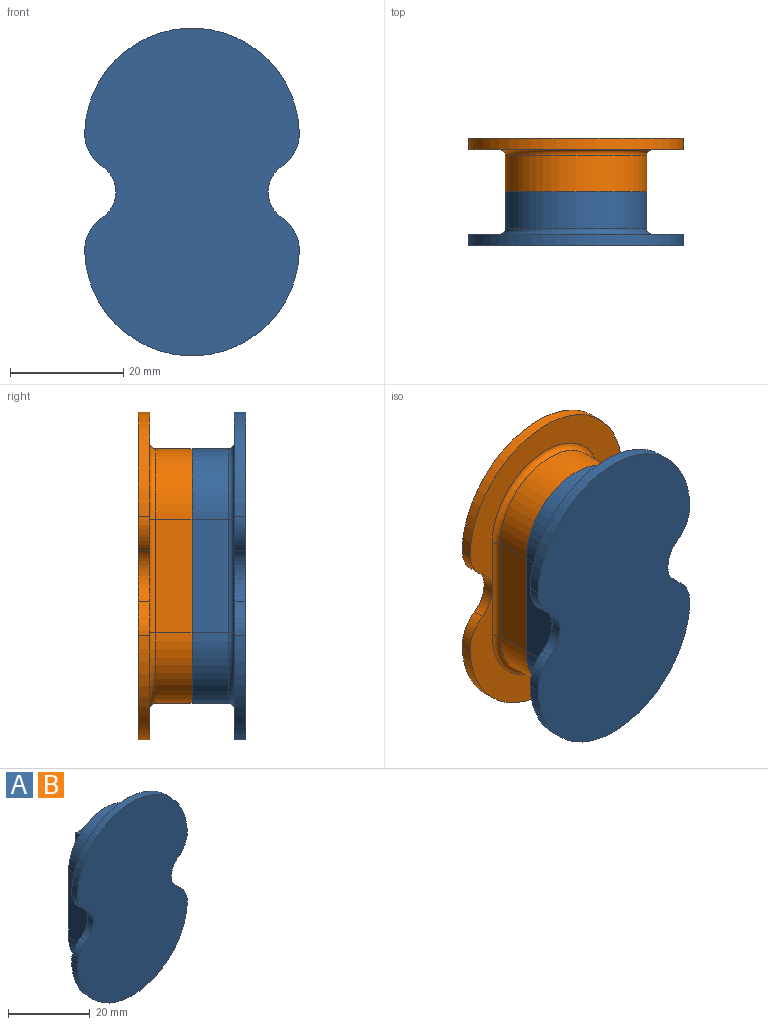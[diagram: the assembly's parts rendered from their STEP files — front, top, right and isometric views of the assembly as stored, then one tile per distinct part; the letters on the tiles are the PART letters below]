
ASSEMBLY  parts=2 mates=1
PART A: 30 faces, bbox 38x14.5x58 mm
  f0: plane 37.99x29mm, normal (0,1,0), area 336.6mm2, adj f17,f21,f22,f23,f24,f25,f26,f29
  f1: plane 45x25mm, normal (0,1,0), area 788.9mm2, adj f2,f3,f4,f5,f6,f7,f8,f9
  f2: plane 20x6.5mm, normal (1,0,0), area 130mm2, adj f1,f3,f5,f22
  f3: cylinder r=12.5mm len=25mm, axis (0,1,0), area 255.3mm2, adj f1,f2,f4,f20
  f4: plane 20x6.5mm, normal (-1,0,0), area 130mm2, adj f1,f3,f5,f21
  f5: cylinder r=12.5mm len=25mm, axis (0,1,0), area 255.3mm2, adj f1,f2,f4,f23
  f6: plane 10x5mm, normal (-1,0,0), area 50mm2, adj f1,f7,f9,f10
  f7: plane 10x5mm, normal (0,0,1), area 50mm2, adj f1,f6,f8,f10
  f8: plane 10x5mm, normal (1,0,0), area 50mm2, adj f1,f7,f9,f10
  f9: plane 10x5mm, normal (0,0,-1), area 50mm2, adj f1,f6,f8,f10
  f10: plane 10x10mm, normal (0,1,0), area 100mm2, adj f6,f7,f8,f9
  f11: plane 10.1x5mm, normal (0,0,-1), area 50.5mm2, adj f1,f12,f14,f15
  f12: plane 10.1x5mm, normal (-1,0,0), area 50.5mm2, adj f1,f11,f13,f15
  f13: plane 10.1x5mm, normal (0,0,1), area 50.5mm2, adj f1,f12,f14,f15
  f14: plane 10.1x5mm, normal (1,0,0), area 50.5mm2, adj f1,f11,f13,f15
  f15: plane 10.1x10.1mm, normal (0,1,0), area 102mm2, adj f11,f12,f13,f14
  f16: plane 37.99x29mm, normal (0,1,0), area 336.6mm2, adj f18,f20,f21,f22,f24,f25,f27,f28
  f17: cylinder r=19mm len=37.98mm, axis (0,1,0), area 117.1mm2, adj f0,f19,f26,f29
  f18: cylinder r=19mm len=37.98mm, axis (0,1,0), area 117.1mm2, adj f16,f19,f27,f28
  f19: plane 58x37.99mm, normal (0,-1,0), area 1785.7mm2, adj f17,f18,f24,f25,f26,f27,f28,f29
  f20: torus R=13.5mm, axis (0,-1,0), area 63.5mm2, adj f3,f16,f21,f22
  f21: cylinder r=1mm len=20mm, axis (0,0,1), area 31.4mm2, adj f0,f4,f16,f20,f23
  f22: cylinder r=1mm len=20mm, axis (0,0,-1), area 31.4mm2, adj f0,f2,f16,f20,f23
  f23: torus R=13.5mm, axis (0,-1,0), area 63.5mm2, adj f0,f5,f21,f22
  f24: cylinder r=5.5mm len=9.11mm, axis (0,-1,0), area 21.5mm2, adj f0,f16,f19,f28,f29
  f25: cylinder r=5.5mm len=9.11mm, axis (0,-1,0), area 21.5mm2, adj f0,f16,f19,f26,f27
  f26: cylinder r=7mm len=6mm, axis (0,1,0), area 14.1mm2, adj f0,f17,f19,f25
  f27: cylinder r=7mm len=6mm, axis (0,-1,0), area 14.1mm2, adj f16,f18,f19,f25
  f28: cylinder r=7mm len=6mm, axis (0,1,0), area 14.1mm2, adj f16,f18,f19,f24
  f29: cylinder r=7mm len=6mm, axis (0,-1,0), area 14.1mm2, adj f0,f17,f19,f24
PART B: same geometry as A
PLACE A rot(axis=(0.05,0.94,-0.33),0deg) t=(0,9.5,0)mm
PLACE B rot(axis=(1,0,0),180deg) t=(0,9.5,0)mm
MATE fastened A.f3 <-> B.f17  axis (0,1,0) through (0,9.5,10)mm
